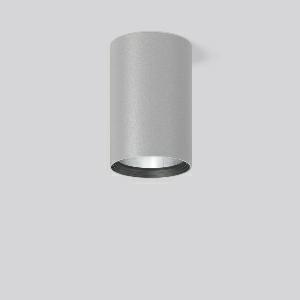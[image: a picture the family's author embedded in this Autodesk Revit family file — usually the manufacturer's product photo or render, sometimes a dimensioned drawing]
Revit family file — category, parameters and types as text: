
# Revit family: heledon_maxi_a_931230_004_1422
name_source: partatom
category: Lighting Fixtures
units: mm (PartAtom-declared; Revit-internal decimal feet)

## family parameters
Cut with Voids When Loaded = No
Host = Face
Light Source = No
Part Type = Normal
Room Calculation Point = No
Round Connector Dimension = Use Diameter
Shared = No

## types (1)
- HELEDON maxi A (1 x LED Modul 932 fresh meat, 2100 lm, 3200)
    Apparent Load = 33 VA
    Approval mark = CE
    CIE Flux Codes = 100 100 100 100 100
    Color Rendering = 90
    Color Temperature = 3200
    Default Elevation = 1800 mm
    Description = Series: HELEDON maxi
Cylindrical surface-mounted downlight. Housing: die-cast aluminium, powder-coated. Internal ceiling frame polycarbonate with bayonet mounting. Black plastic ring and recessed LED to prevent glare from the side. Optical assembly with reflector made of MIRO-Silver with 98% total light reflection for outstanding efficiency - can be changed without tools. Special LED for illumination of meat included. Suitable for Ceiling mounting. Easy installation with a separate ceiling frame with bayonet mounting and plug connection. Driver integrated. Connected via plug-in connector. High quality converter without flickering and stroboscopic effect. The following accessories can be mounted without use of tools: interchangeable lenses, decorative glasses, honeycomb louvre, clear and frosted diffusers, white interchangeable plastic ring. 
Colour: silver
Diameter: 123 mm
Height: 183 mm
Lamp: LED
Socket: without socket
Colour temperature: fresh meat
System power: 33 W
Rated luminous flux: 2100 lm
Luminous efficiency: 64 lm/W
Control gear: Regulated power supply
Protection class: I
Type of protection: IP 20
    Height = 183 mm
    Lamp = 1 x LED Modul 932 fresh meat
    Lamp Light Flux = 2100 lm
    Lamp count = 1
    Length = 123 mm
    Lifetime = 50000 h
    Luminous efficacy = 64 lm/W
    Manufacturer = RZB
    ModVariant = No
    Model = 931230.004
    Mounting Place = Ceiling
    Mounting Type = Surface mounted
    Number of Poles = 1
    OnlyDefault = Yes
    Power Factor = 1
    Product Name = HELEDON maxi A
    Product group = Surface mounted downlights
    ProductGroupID = 302
    Protection Class = Protection class I
    Protection Degree = IP 20
    RLX_Detail_Level = 1
    RLX_Emergency_Light_Flux = 0 lm
    RLX_Emergency_Type = 0
    RLX_Emergency_Type_DB = No
    RlxData = <blob elided: 99297 chars, md5=c21be219>
    Socket = socket
    Standby Power = 0 W
    System Light Flux = 2100 lm
    System Power = 33 W
    Type Comments = Product without accessories
    Type Image = 931192.004.jpg
    URL = http://relux.com
    VarID = ---
    Voltage = 230 V
    Voltage Range = 220-240 V
    Weight = 0.00 kg
    Width = 0 mm  [stored 0 ft]

note: [stored X ft] marks values corroborated as IEEE doubles in the binary element streams (Revit-internal decimal feet)

## geometry (parser evidence)
native form markers: Blend x4, Sweep x10
no freeform markers — native parametric forms only
